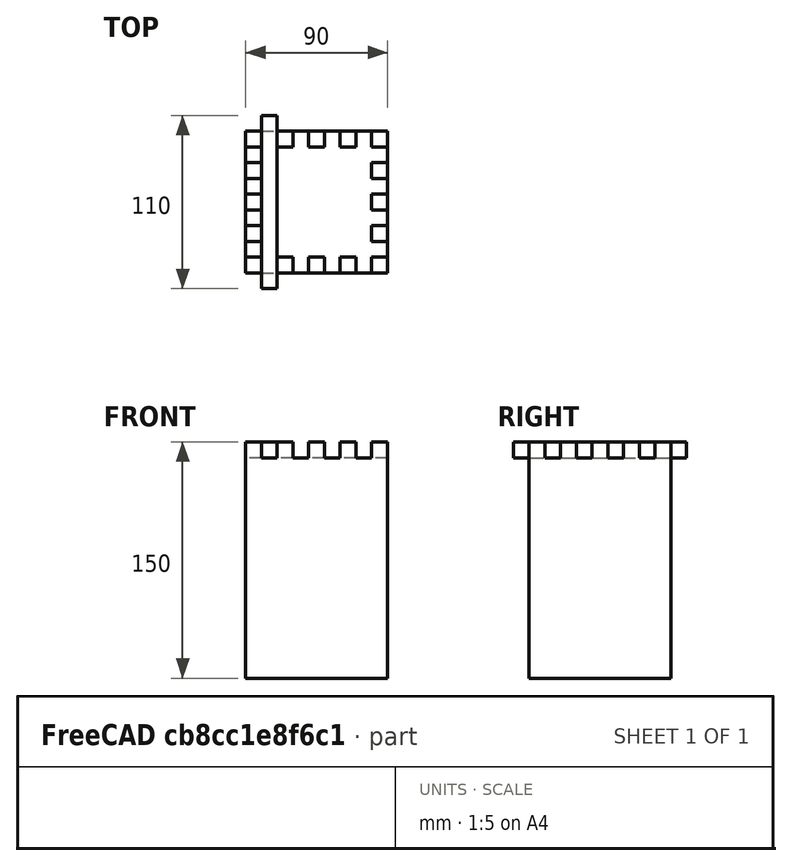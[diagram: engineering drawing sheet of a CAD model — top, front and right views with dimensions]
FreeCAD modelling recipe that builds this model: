
FCSTD DOCUMENT  (FreeCAD 1.0R39319 (Git))
Label: ojt1_t10r02_tower
License: All rights reserved
LicenseURL: https://en.wikipedia.org/wiki/All_rights_reserved
objects: Part::Box×4, Part::Cut×3, Part::FeaturePython×2
note: 7 computed .brp shape members not serialized (recipe doc carries the construction recipe); baked Part::Feature solids carry a one-line shape summary decoded from their .brp

FEATURE [Part::Box] Box  label="Cube"
  AttacherType = Attacher::AttachEngine3D
  Height = 150
  Length = 90
  Width = 90
FEATURE [Part::Box] Box001  label="Cube001"
  AttacherType = Attacher::AttachEngine3D
  Height = 10
  Length = 10
  Placement = pos=(10,-10,140) rot=(0,0,1;0rad)
  Width = 110
FEATURE [Part::FeaturePython] Array  # Draft array (typed FeaturePython)
  AlwaysSyncPlacement = false
  Angle = 360
  ArrayType = 0
  Axis = (0,0,1)
  Base = -> Box001
  Center = (0,0,0)
  Count = 4
  ExpandArray = false
  Fuse = false
  IntervalAxis = (0,0,0)
  IntervalX = (20,0,0)
  IntervalY = (0,20,0)
  IntervalZ = (0,0,20)
  NumberCircles = 3
  NumberPolar = 5
  NumberX = 4
  NumberY = 1
  NumberZ = 1
  PlacementList = 4 placements: arithmetic series from (10,-10,140) step (20,0,0) to (70,-10,140)
  RadialDistance = 50
  ScaleList = (4) [(1,1,1),(1,1,1),(1,1,1),(1,1,1)]
  Symmetry = 1
  TangentialDistance = 25
FEATURE [Part::Box] Box002  label="Cube002"
  AttacherType = Attacher::AttachEngine3D
  Height = 10
  Length = 10
  Placement = pos=(10,-10,140) rot=(0,0,1;0rad)
  Width = 110
FEATURE [Part::FeaturePython] Array001  # Draft array (typed FeaturePython)
  AlwaysSyncPlacement = false
  Angle = 360
  ArrayType = 0
  Axis = (0,0,1)
  Base = -> Box002
  Center = (0,0,0)
  Count = 4
  ExpandArray = false
  Fuse = false
  IntervalAxis = (0,0,0)
  IntervalX = (20,0,0)
  IntervalY = (0,20,0)
  IntervalZ = (0,0,20)
  NumberCircles = 3
  NumberPolar = 5
  NumberX = 4
  NumberY = 1
  NumberZ = 1
  Placement = pos=(90,0,0) rot=(0,0,1;1.5708rad)
  PlacementList = 4 placements: arithmetic series from (10,-10,140) step (20,0,0) to (70,-10,140)
  RadialDistance = 50
  ScaleList = (4) [(1,1,1),(1,1,1),(1,1,1),(1,1,1)]
  Symmetry = 1
  TangentialDistance = 25
FEATURE [Part::Cut] Cut
  Base = -> Box
  Refine = true
  Tool = -> Array
FEATURE [Part::Cut] Cut001
  Base = -> Cut
  Refine = true
  Tool = -> Array001
FEATURE [Part::Box] Box003  label="Cube003"
  AttacherType = Attacher::AttachEngine3D
  Height = 10
  Length = 50
  Placement = pos=(20,20,140) rot=(0,0,1;0rad)
  Width = 50
FEATURE [Part::Cut] Cut002
  Base = -> Cut001
  Refine = true
  Tool = -> Box003
